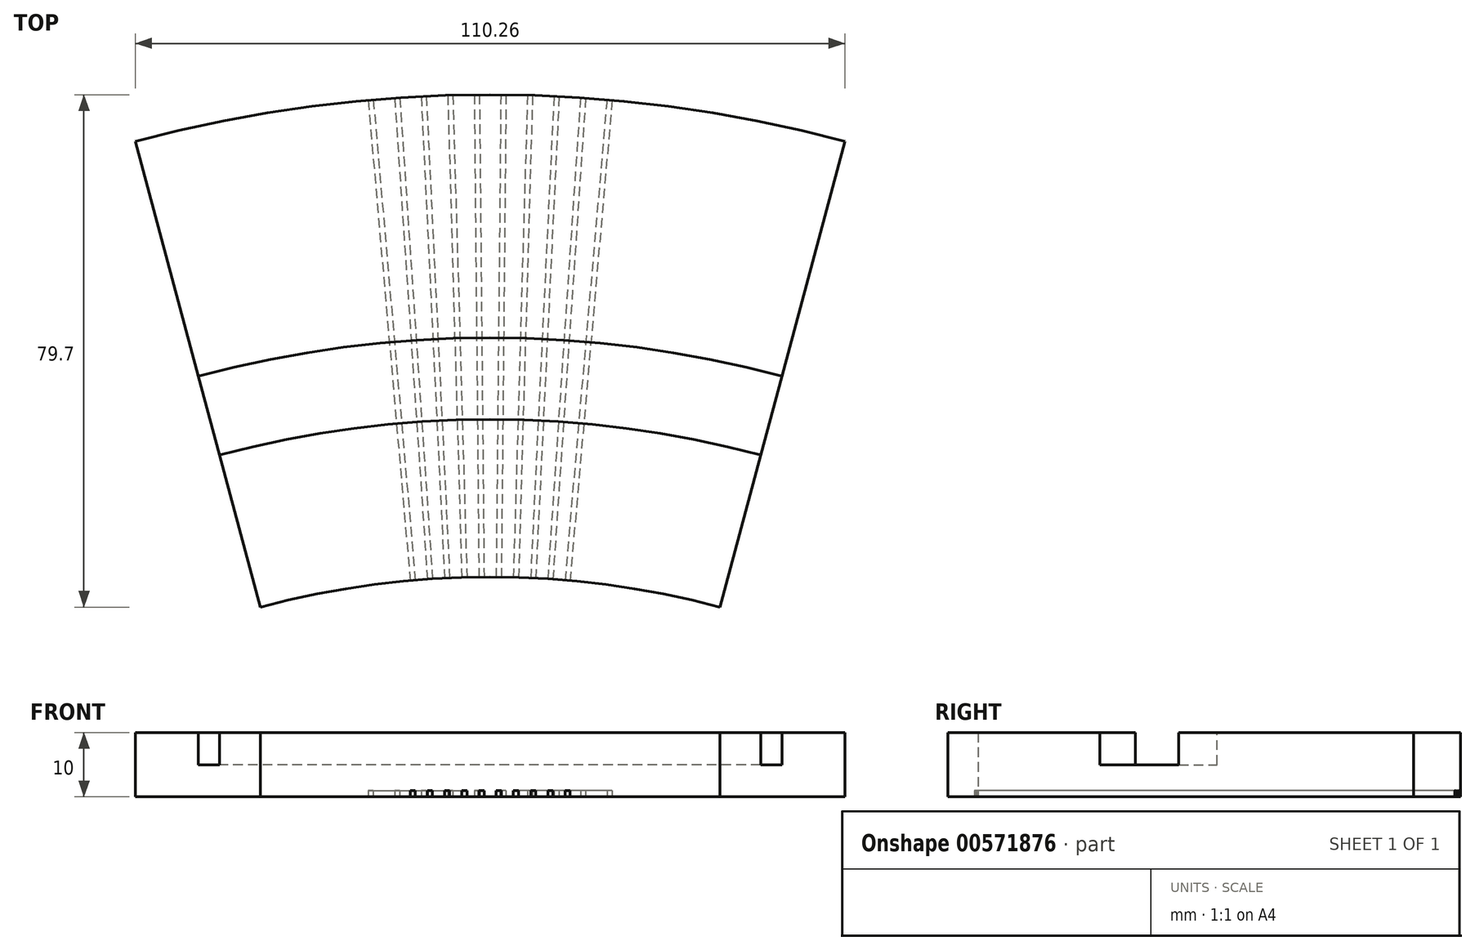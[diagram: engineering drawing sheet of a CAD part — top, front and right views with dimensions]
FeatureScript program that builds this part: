
annotation { "Feature Type Name" : "Feature", "Feature Type Description" : "" }
export const myFeature = defineFeature(function(context is Context, id is Id, definition is map)
    precondition{}
    {
        {
            var Q0;
            Q0=qCreatedBy(makeId("Top.planeOp"),FACE);
            var sketch = newSketch(context, id + "F0", { "sketchPlane" : qUnion([Q0])});
            skCircle(sketch, "E0", {"center": v(0, -138) * mm, "radius": 75 * mm});
            skLineSegment(sketch, "E1", {"start": v(0, -138) * mm, "end": v(17.37, 60.5) * mm});
            skLineSegment(sketch, "E2", {"start": v(0, -138) * mm, "end": v(0, 80.9) * mm});
            skLineSegment(sketch, "E3.anchor1", {"start": v(0, -138) * mm, "end": v(17.37, 60.5) * mm, "construction": true});
            skPoint(sketch, "E4.middle", {"position": v(17.37, 60.5) * mm});
            skPoint(sketch, "E5.middle", {"position": v(9.63, -27.92) * mm});
            skLineSegment(sketch, "E6.bottom", {"start": v(21.14, 99.06) * mm, "end": v(20.34, 99.13) * mm});
            skLineSegment(sketch, "E6.top", {"start": v(-4.55, -194.62) * mm, "end": v(-5.35, -194.55) * mm});
            skLineSegment(sketch, "E6.left", {"start": v(21.14, 99.06) * mm, "end": v(-4.55, -194.62) * mm});
            skLineSegment(sketch, "E6.right", {"start": v(20.34, 99.13) * mm, "end": v(-5.35, -194.55) * mm});
            skPoint(sketch, "E6.middle", {"position": v(7.9, -47.75) * mm});
            skCircle(sketch, "E7", {"center": v(0, -138) * mm, "radius": 138 * mm});
            skLineSegment(sketch, "E8.1.0", {"start": v(15.74, 99.48) * mm, "end": v(-4.25, -194.65) * mm});
            skLineSegment(sketch, "E8.1.1", {"start": v(16.54, 99.42) * mm, "end": v(-3.45, -194.7) * mm});
            skLineSegment(sketch, "E8.1.2", {"start": v(16.54, 99.42) * mm, "end": v(15.74, 99.48) * mm});
            skLineSegment(sketch, "E8.1.3", {"start": v(-3.45, -194.7) * mm, "end": v(-4.25, -194.65) * mm});
            skLineSegment(sketch, "E8.2.0", {"start": v(11.13, 99.74) * mm, "end": v(-3.15, -194.72) * mm});
            skLineSegment(sketch, "E8.2.1", {"start": v(11.93, 99.7) * mm, "end": v(-2.35, -194.76) * mm});
            skLineSegment(sketch, "E8.2.2", {"start": v(11.93, 99.7) * mm, "end": v(11.13, 99.74) * mm});
            skLineSegment(sketch, "E8.2.3", {"start": v(-2.35, -194.76) * mm, "end": v(-3.15, -194.72) * mm});
            skLineSegment(sketch, "E9.0.3.0", {"start": v(6.52, 99.91) * mm, "end": v(-2.05, -194.77) * mm});
            skLineSegment(sketch, "E9.3.3.0", {"start": v(7.32, 99.89) * mm, "end": v(-1.25, -194.8) * mm});
            skLineSegment(sketch, "E9.6.3.0", {"start": v(7.32, 99.89) * mm, "end": v(6.52, 99.91) * mm});
            skLineSegment(sketch, "E9.9.3.0", {"start": v(-1.25, -194.8) * mm, "end": v(-2.05, -194.77) * mm});
            skLineSegment(sketch, "E9.0.4.0", {"start": v(1.9, 100) * mm, "end": v(-0.95, -194.8) * mm});
            skLineSegment(sketch, "E9.3.4.0", {"start": v(2.7, 99.98) * mm, "end": v(-0.15, -194.8) * mm});
            skLineSegment(sketch, "E9.6.4.0", {"start": v(2.7, 99.98) * mm, "end": v(1.9, 100) * mm});
            skLineSegment(sketch, "E9.9.4.0", {"start": v(-0.15, -194.8) * mm, "end": v(-0.95, -194.8) * mm});
            skLineSegment(sketch, "E9.0.5.0", {"start": v(-2.7, 99.98) * mm, "end": v(0.15, -194.8) * mm});
            skLineSegment(sketch, "E9.3.5.0", {"start": v(-1.9, 100) * mm, "end": v(0.95, -194.8) * mm});
            skLineSegment(sketch, "E9.6.5.0", {"start": v(-1.9, 100) * mm, "end": v(-2.7, 99.98) * mm});
            skLineSegment(sketch, "E9.9.5.0", {"start": v(0.95, -194.8) * mm, "end": v(0.15, -194.8) * mm});
            skLineSegment(sketch, "E9.0.6.0", {"start": v(-7.32, 99.89) * mm, "end": v(1.25, -194.8) * mm});
            skLineSegment(sketch, "E9.3.6.0", {"start": v(-6.52, 99.91) * mm, "end": v(2.05, -194.77) * mm});
            skLineSegment(sketch, "E9.6.6.0", {"start": v(-6.52, 99.91) * mm, "end": v(-7.32, 99.89) * mm});
            skLineSegment(sketch, "E9.9.6.0", {"start": v(2.05, -194.77) * mm, "end": v(1.25, -194.8) * mm});
            skLineSegment(sketch, "E9.0.7.0", {"start": v(-11.93, 99.7) * mm, "end": v(2.35, -194.76) * mm});
            skLineSegment(sketch, "E9.3.7.0", {"start": v(-11.13, 99.74) * mm, "end": v(3.15, -194.72) * mm});
            skLineSegment(sketch, "E9.6.7.0", {"start": v(-11.13, 99.74) * mm, "end": v(-11.93, 99.7) * mm});
            skLineSegment(sketch, "E9.9.7.0", {"start": v(3.15, -194.72) * mm, "end": v(2.35, -194.76) * mm});
            skLineSegment(sketch, "E9.0.8.0", {"start": v(-16.54, 99.42) * mm, "end": v(3.45, -194.7) * mm});
            skLineSegment(sketch, "E9.3.8.0", {"start": v(-15.74, 99.48) * mm, "end": v(4.25, -194.65) * mm});
            skLineSegment(sketch, "E9.6.8.0", {"start": v(-15.74, 99.48) * mm, "end": v(-16.54, 99.42) * mm});
            skLineSegment(sketch, "E9.9.8.0", {"start": v(4.25, -194.65) * mm, "end": v(3.45, -194.7) * mm});
            skLineSegment(sketch, "E9.0.9.0", {"start": v(-21.14, 99.06) * mm, "end": v(4.55, -194.62) * mm});
            skLineSegment(sketch, "E9.3.9.0", {"start": v(-20.34, 99.13) * mm, "end": v(5.35, -194.55) * mm});
            skLineSegment(sketch, "E9.6.9.0", {"start": v(-20.34, 99.13) * mm, "end": v(-21.14, 99.06) * mm});
            skLineSegment(sketch, "E9.9.9.0", {"start": v(5.35, -194.55) * mm, "end": v(4.55, -194.62) * mm});
            skSolve(sketch);
        }
        {
            var Q0;
            Q0=qCreatedBy(makeId("Right.planeOp"),FACE);
            var sketch = newSketch(context, id + "F1", { "sketchPlane" : qUnion([Q0])});
            skLineSegment(sketch, "E10.bottom", {"start": v(0, 0) * mm, "end": v(75, 0) * mm});
            skLineSegment(sketch, "E10.top", {"start": v(0, 10) * mm, "end": v(75, 10) * mm});
            skLineSegment(sketch, "E10.left", {"start": v(0, 0) * mm, "end": v(0, 10) * mm});
            skLineSegment(sketch, "E10.right", {"start": v(75, 0) * mm, "end": v(75, 10) * mm});
            skLineSegment(sketch, "E11", {"start": v(-138, 0) * mm, "end": v(-138, 50.14) * mm});
            skSolve(sketch);
        }
        {
            var Q0;
            Q0=makeQuery(id+"F1.imprint","IMPRINT",FACE,{"disambiguationData":[TD([[makeQuery(id+"F1.imprint","IMPRINT",EDGE,{"derivedFrom":sQuery(id+"F1.wireOp",EDGE,"E10.bottom")}),1.0]])]});
            var Q1;
            Q1=sQuery(id+"F1.wireOp",EDGE,"E11");
            revolve(context, id + "F2", {"entities" : qUnion([Q0]), "axis" : qUnion([Q1]), "revolveType" : RevolveType.SYMMETRIC, "angle" : 30 * degree});
        }
        {
            var Q0;
            {var subQ5=sQuery(id+"F0.wireOp",EDGE,"E9.6.9.0");Q0=makeQuery(id+"F0.imprint","IMPRINT",FACE,{"disambiguationData":[TD([[makeQuery(id+"F0.imprint","IMPRINT",EDGE,{"derivedFrom":subQ5}),1.0]])]});}
            var Q1;
            {var subQ5=sQuery(id+"F0.wireOp",EDGE,"E9.6.8.0");Q1=makeQuery(id+"F0.imprint","IMPRINT",FACE,{"disambiguationData":[TD([[makeQuery(id+"F0.imprint","IMPRINT",EDGE,{"derivedFrom":subQ5}),1.0]])]});}
            var Q2;
            {var subQ5=sQuery(id+"F0.wireOp",EDGE,"E9.6.7.0");Q2=makeQuery(id+"F0.imprint","IMPRINT",FACE,{"disambiguationData":[TD([[makeQuery(id+"F0.imprint","IMPRINT",EDGE,{"derivedFrom":subQ5}),1.0]])]});}
            var Q3;
            {var subQ5=sQuery(id+"F0.wireOp",EDGE,"E9.6.6.0");Q3=makeQuery(id+"F0.imprint","IMPRINT",FACE,{"disambiguationData":[TD([[makeQuery(id+"F0.imprint","IMPRINT",EDGE,{"derivedFrom":subQ5}),1.0]])]});}
            var Q4;
            {var subQ5=sQuery(id+"F0.wireOp",EDGE,"E9.6.5.0");Q4=makeQuery(id+"F0.imprint","IMPRINT",FACE,{"disambiguationData":[TD([[makeQuery(id+"F0.imprint","IMPRINT",EDGE,{"derivedFrom":subQ5}),1.0]])]});}
            var Q5;
            {var subQ5=sQuery(id+"F0.wireOp",EDGE,"E9.6.4.0");Q5=makeQuery(id+"F0.imprint","IMPRINT",FACE,{"disambiguationData":[TD([[makeQuery(id+"F0.imprint","IMPRINT",EDGE,{"derivedFrom":subQ5}),1.0]])]});}
            var Q6;
            {var subQ5=sQuery(id+"F0.wireOp",EDGE,"E9.6.3.0");Q6=makeQuery(id+"F0.imprint","IMPRINT",FACE,{"disambiguationData":[TD([[makeQuery(id+"F0.imprint","IMPRINT",EDGE,{"derivedFrom":subQ5}),1.0]])]});}
            var Q7;
            {var subQ5=sQuery(id+"F0.wireOp",EDGE,"E8.2.2");Q7=makeQuery(id+"F0.imprint","IMPRINT",FACE,{"disambiguationData":[TD([[makeQuery(id+"F0.imprint","IMPRINT",EDGE,{"derivedFrom":subQ5}),1.0]])]});}
            var Q8;
            {var subQ5=sQuery(id+"F0.wireOp",EDGE,"E8.1.2");Q8=makeQuery(id+"F0.imprint","IMPRINT",FACE,{"disambiguationData":[TD([[makeQuery(id+"F0.imprint","IMPRINT",EDGE,{"derivedFrom":subQ5}),1.0]])]});}
            var Q9;
            {var subQ4=sQuery(id+"F0.wireOp",EDGE,"E6.bottom");Q9=makeQuery(id+"F0.imprint","IMPRINT",FACE,{"disambiguationData":[TD([[makeQuery(id+"F0.imprint","IMPRINT",EDGE,{"derivedFrom":subQ4}),1.0]])]});}
            extrude(context, id + "F3", {"entities" : qUnion([Q0, Q1, Q2, Q3, Q4, Q5, Q6, Q7, Q8, Q9]), "operationType" : NewBodyOperationType.REMOVE, "depth" : 1 * mm, "offsetDistance" : 25 * mm});
        }
        {
            var Q0;
            Q0=makeQuery(id+"F2.opRevolve","SWEPT_FACE",FACE,{"disambiguationData":[OSD([sQuery(id+"F1.wireOp",EDGE,"E10.top")])]});
            var sketch = newSketch(context, id + "F4", { "sketchPlane" : qUnion([Q0])});
            skCircle(sketch, "E12", {"center": v(0, -138) * mm, "radius": 162.5 * mm});
            skCircle(sketch, "E13", {"center": v(0, -138) * mm, "radius": 175.2 * mm});
            skSolve(sketch);
        }
        {
            var Q0;
            {var subQ0=sQuery(id+"F4.wireOp",EDGE,"E12");var subQ1=sQuery(id+"F1.wireOp",EDGE,"E10.top");var subQ2=makeQuery(id+"F2.opRevolve","CAP_EDGE",EDGE,{"disambiguationData":[OSD([subQ1])],"isStart":true});var subQ3=makeQuery(id+"F4.imprint","INTERSECT",VERTEX,{"derivedFrom":[subQ2,subQ0]});Q0=makeQuery(id+"F4.imprint","IMPRINT",FACE,{"disambiguationData":[TD([[makeQuery(id+"F4.imprint","IMPRINT",EDGE,{"disambiguationData":[TD([[subQ3,1.0]])],"derivedFrom":subQ0}),-1.0]])]});}
            var Q1;
            {var subQ0=sQuery(id+"F4.wireOp",EDGE,"E12");var subQ1=sQuery(id+"F1.wireOp",EDGE,"E10.top");var subQ2=makeQuery(id+"F2.opRevolve","CAP_EDGE",EDGE,{"disambiguationData":[OSD([subQ1])],"isStart":true});var subQ3=makeQuery(id+"F4.imprint","INTERSECT",VERTEX,{"derivedFrom":[subQ2,subQ0]});Q1=makeQuery(id+"F4.imprint","IMPRINT",FACE,{"disambiguationData":[TD([[makeQuery(id+"F4.imprint","IMPRINT",EDGE,{"disambiguationData":[TD([[subQ3,-1.0]])],"derivedFrom":subQ0}),-1.0]])]});}
            extrude(context, id + "F5", {"entities" : qUnion([Q0, Q1]), "operationType" : NewBodyOperationType.REMOVE, "oppositeDirection" : true, "depth" : 5 * mm, "offsetDistance" : 25 * mm});
        }
    });
